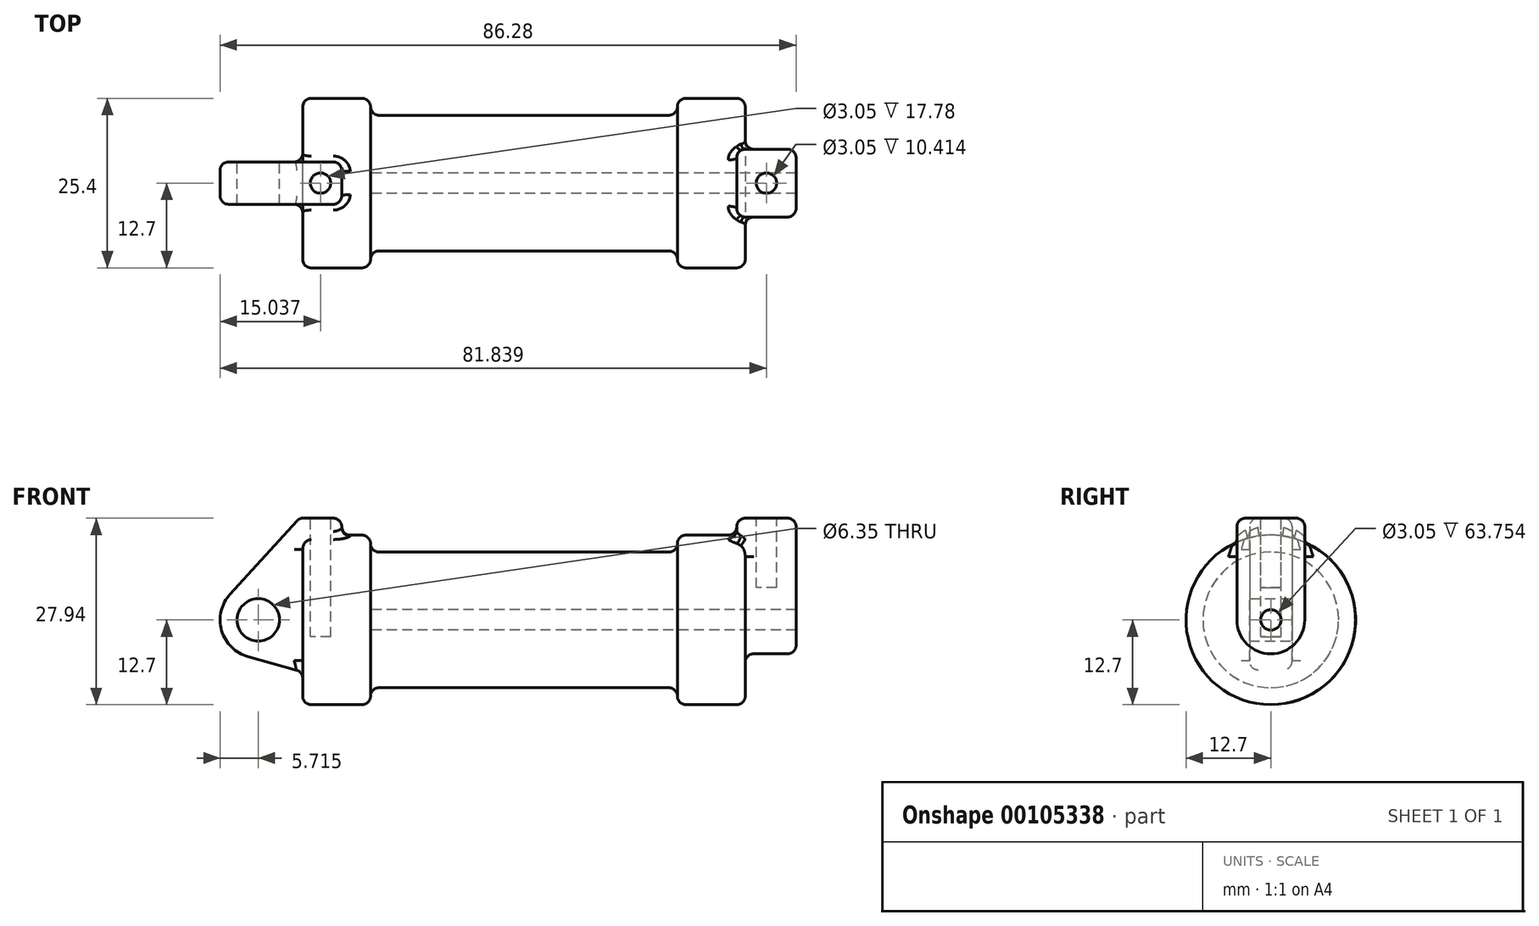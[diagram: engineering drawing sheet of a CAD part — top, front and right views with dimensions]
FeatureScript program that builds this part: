
annotation { "Feature Type Name" : "Feature", "Feature Type Description" : "" }
export const myFeature = defineFeature(function(context is Context, id is Id, definition is map)
    precondition{}
    {
        {
            var Q0;
            Q0=qCreatedBy(makeId("Front.planeOp"),FACE);
            var sketch = newSketch(context, id + "F0", { "sketchPlane" : qUnion([Q0])});
            skLineSegment(sketch, "E0", {"start": v(0, 0) * mm, "end": v(0, 12.7) * mm});
            skLineSegment(sketch, "E1", {"start": v(0, 12.7) * mm, "end": v(10.16, 12.7) * mm});
            skLineSegment(sketch, "E2", {"start": v(10.16, 12.7) * mm, "end": v(10.16, 10.16) * mm});
            skLineSegment(sketch, "E3", {"start": v(10.16, 10.16) * mm, "end": v(56.13, 10.16) * mm});
            skLineSegment(sketch, "E4", {"start": v(56.13, 10.16) * mm, "end": v(56.13, 12.7) * mm});
            skLineSegment(sketch, "E5", {"start": v(56.13, 12.7) * mm, "end": v(66.3, 12.7) * mm});
            skLineSegment(sketch, "E6", {"start": v(66.3, 12.7) * mm, "end": v(66.3, 0) * mm});
            skLineSegment(sketch, "E7", {"start": v(66.3, 0) * mm, "end": v(0, 0) * mm});
            skLineSegment(sketch, "E8", {"start": v(5.84, 15.24) * mm, "end": v(-0.5, 15.24) * mm});
            skLineSegment(sketch, "E9", {"start": v(-0.5, 15.24) * mm, "end": v(-10.88, 3.85) * mm});
            skLineSegment(sketch, "E10", {"start": v(0, 0) * mm, "end": v(-6.65, 0) * mm});
            skCircle(sketch, "E11", {"center": v(-6.65, 0) * mm, "radius": 5.72 * mm});
            skCircle(sketch, "E12", {"center": v(-6.65, 0) * mm, "radius": 3.18 * mm});
            skLineSegment(sketch, "E13", {"start": v(5.84, 15.24) * mm, "end": v(5.84, -9.4) * mm});
            skLineSegment(sketch, "E14", {"start": v(5.84, -9.4) * mm, "end": v(-8.18, -5.5) * mm});
            skSolve(sketch);
        }
        {
            var Q0;
            {var subQ0=sQuery(id+"F0.wireOp",EDGE,"E2");Q0=makeQuery(id+"F0.imprint","IMPRINT",FACE,{"disambiguationData":[TD([[makeQuery(id+"F0.imprint","IMPRINT",EDGE,{"derivedFrom":subQ0}),-1.0]])]});}
            var Q1;
            {var subQ0=sQuery(id+"F0.wireOp",EDGE,"E0");Q1=makeQuery(id+"F0.imprint","IMPRINT",FACE,{"disambiguationData":[TD([[makeQuery(id+"F0.imprint","IMPRINT",EDGE,{"derivedFrom":subQ0}),-1.0]])]});}
            var Q2;
            Q2=sQuery(id+"F0.wireOp",EDGE,"E7");
            revolve(context, id + "F1", {"entities" : qUnion([Q0, Q1]), "axis" : qUnion([Q2]), "revolveType" : RevolveType.FULL});
        }
        {
            var Q0;
            {var subQ3=sQuery(id+"F0.wireOp",EDGE,"E0");Q0=makeQuery(id+"F0.imprint","IMPRINT",FACE,{"disambiguationData":[TD([[makeQuery(id+"F0.imprint","IMPRINT",EDGE,{"derivedFrom":subQ3}),1.0]])]});}
            var Q1;
            {var subQ4=sQuery(id+"F0.wireOp",EDGE,"E12");Q1=makeQuery(id+"F0.imprint","IMPRINT",FACE,{"disambiguationData":[TD([[makeQuery(id+"F0.imprint","IMPRINT",EDGE,{"derivedFrom":subQ4}),-1.0]])]});}
            var Q2;
            {var subQ0=sQuery(id+"F0.wireOp",EDGE,"E14");Q2=makeQuery(id+"F0.imprint","IMPRINT",FACE,{"disambiguationData":[TD([[makeQuery(id+"F0.imprint","IMPRINT",EDGE,{"derivedFrom":subQ0}),-1.0]])]});}
            var Q3;
            {var subQ0=sQuery(id+"F0.wireOp",EDGE,"E0");Q3=makeQuery(id+"F0.imprint","IMPRINT",FACE,{"disambiguationData":[TD([[makeQuery(id+"F0.imprint","IMPRINT",EDGE,{"derivedFrom":subQ0}),-1.0]])]});}
            extrude(context, id + "F2", {"entities" : qUnion([Q0, Q1, Q2, Q3]), "operationType" : NewBodyOperationType.ADD, "endBound" : BoundingType.SYMMETRIC, "depth" : 6.35 * mm});
        }
        {
            var Q0;
            Q0=makeQuery(id+"F1.opRevolve","SWEPT_FACE",FACE,{"disambiguationData":[OSD([sQuery(id+"F0.wireOp",EDGE,"E6")])]});
            var sketch = newSketch(context, id + "F3", { "sketchPlane" : qUnion([Q0])});
            skCircle(sketch, "E15", {"center": v(0, 0) * mm, "radius": 1.52 * mm});
            skCircle(sketch, "E16", {"center": v(0, 0) * mm, "radius": 5.08 * mm});
            skLineSegment(sketch, "E17", {"start": v(5.08, 0) * mm, "end": v(5.08, 15.24) * mm});
            skLineSegment(sketch, "E18", {"start": v(-5.08, 0) * mm, "end": v(-5.08, 15.24) * mm});
            skLineSegment(sketch, "E19", {"start": v(-5.08, 15.24) * mm, "end": v(5.08, 15.24) * mm});
            skSolve(sketch);
        }
        {
            var Q0;
            {var subQ0=sQuery(id+"F3.wireOp",EDGE,"E19");Q0=makeQuery(id+"F3.imprint","IMPRINT",FACE,{"disambiguationData":[TD([[makeQuery(id+"F3.imprint","IMPRINT",EDGE,{"derivedFrom":subQ0}),-1.0]])]});}
            var Q1;
            {var subQ0=sQuery(id+"F3.wireOp",EDGE,"E17");var subQ1=sQuery(id+"F3.wireOp",EDGE,"E16");var subQ2=makeQuery(id+"F3.imprint","INTERSECT",VERTEX,{"derivedFrom":[subQ1,subQ0]});Q1=makeQuery(id+"F3.imprint","IMPRINT",FACE,{"disambiguationData":[TD([[makeQuery(id+"F3.imprint","IMPRINT",EDGE,{"disambiguationData":[TD([[subQ2,-1.0]])],"derivedFrom":subQ1}),-1.0]])]});}
            var Q2;
            Q2=makeQuery(id+"F3.imprint","IMPRINT",FACE,{"disambiguationData":[TD([[makeQuery(id+"F3.imprint","IMPRINT",EDGE,{"derivedFrom":sQuery(id+"F3.wireOp",EDGE,"E15")}),-1.0]])]});
            extrude(context, id + "F4", {"entities" : qUnion([Q0, Q1, Q2]), "depth" : 7.62 * mm, "hasSecondDirection" : true, "secondDirectionOppositeDirection" : true, "secondDirectionDepth" : 1.27 * mm});
        }
        {
            var Q0;
            Q0=makeQuery(id+"F4.opExtrude","SWEPT_BODY",BODY,{"disambiguationData":[OSD([sQuery(id+"F3.wireOp",EDGE,"E15"),sQuery(id+"F3.wireOp",EDGE,"E16"),sQuery(id+"F3.wireOp",EDGE,"E17"),sQuery(id+"F3.wireOp",EDGE,"E18"),sQuery(id+"F3.wireOp",EDGE,"E19")])]});
            var Q1;
            Q1=makeQuery(id+"F1.opRevolve","SWEPT_BODY",BODY,{"disambiguationData":[OSD([sQuery(id+"F0.wireOp",EDGE,"E0"),sQuery(id+"F0.wireOp",EDGE,"E1"),sQuery(id+"F0.wireOp",EDGE,"E2"),sQuery(id+"F0.wireOp",EDGE,"E3"),sQuery(id+"F0.wireOp",EDGE,"E4"),sQuery(id+"F0.wireOp",EDGE,"E5"),sQuery(id+"F0.wireOp",EDGE,"E6"),sQuery(id+"F0.wireOp",EDGE,"E7")])]});
            booleanBodies(context, id + "F5", {"operationType" : BooleanOperationType.UNION, "tools" : qUnion([Q0, Q1])});
        }
        {
            var Q0;
            Q0=makeQuery(id+"F3.imprint","IMPRINT",FACE,{"disambiguationData":[TD([[makeQuery(id+"F3.imprint","IMPRINT",EDGE,{"derivedFrom":sQuery(id+"F3.wireOp",EDGE,"E15")}),1.0]])]});
            var Q1;
            Q1=makeQuery(id+"F1.opRevolve","SWEPT_FACE",FACE,{"disambiguationData":[OSD([sQuery(id+"F0.wireOp",EDGE,"E2")])]});
            extrude(context, id + "F6", {"entities" : qUnion([Q0]), "operationType" : NewBodyOperationType.REMOVE, "endBound" : BoundingType.UP_TO_SURFACE, "oppositeDirection" : true, "endBoundEntityFace" : qUnion([Q1]), "depth" : 25.4 * mm});
        }
        {
            var Q0;
            Q0=makeQuery(id+"F4.opExtrude","SWEPT_FACE",FACE,{"disambiguationData":[OSD([sQuery(id+"F3.wireOp",EDGE,"E19")])]});
            var sketch = newSketch(context, id + "F7", { "sketchPlane" : qUnion([Q0])});
            skLineSegment(sketch, "E20", {"start": v(65.02, 0) * mm, "end": v(73.91, 0) * mm, "construction": true});
            skLineSegment(sketch, "E21", {"start": v(69.47, 5.08) * mm, "end": v(69.47, -5.08) * mm, "construction": true});
            skCircle(sketch, "E22", {"center": v(69.47, 0) * mm, "radius": 1.52 * mm});
            skLineSegment(sketch, "E23.0.0", {"start": v(5.84, 3.18) * mm, "end": v(-0.5, 3.18) * mm});
            skLineSegment(sketch, "E23.0.1", {"start": v(-0.5, 3.17) * mm, "end": v(-0.5, -3.18) * mm});
            skLineSegment(sketch, "E23.0.2", {"start": v(-0.5, -3.18) * mm, "end": v(5.84, -3.18) * mm});
            skLineSegment(sketch, "E23.0.3", {"start": v(5.84, -3.18) * mm, "end": v(5.84, 3.17) * mm});
            skLineSegment(sketch, "E24", {"start": v(-0.5, 0) * mm, "end": v(5.84, 0) * mm, "construction": true});
            skLineSegment(sketch, "E25", {"start": v(2.67, 3.18) * mm, "end": v(2.67, -3.18) * mm, "construction": true});
            skCircle(sketch, "E26", {"center": v(2.67, 0) * mm, "radius": 1.52 * mm});
            skSolve(sketch);
        }
        {
            var Q0;
            Q0=makeQuery(id+"F7.imprint","IMPRINT",FACE,{"disambiguationData":[TD([[makeQuery(id+"F7.imprint","IMPRINT",EDGE,{"derivedFrom":sQuery(id+"F7.wireOp",EDGE,"E26")}),1.0]])]});
            var Q1;
            Q1=sQuery(id+"F7.wireOp",EDGE,"E26");
            extrude(context, id + "F8", {"entities" : qUnion([Q0]), "operationType" : NewBodyOperationType.REMOVE, "surfaceEntities" : qUnion([Q1]), "oppositeDirection" : true, "depth" : 17.78 * mm});
        }
        {
            var Q0;
            Q0=makeQuery(id+"F7.imprint","IMPRINT",FACE,{"disambiguationData":[TD([[makeQuery(id+"F7.imprint","IMPRINT",EDGE,{"derivedFrom":sQuery(id+"F7.wireOp",EDGE,"E22")}),1.0]])]});
            var Q1;
            Q1=sQuery(id+"F7.wireOp",EDGE,"E22");
            extrude(context, id + "F9", {"entities" : qUnion([Q0]), "operationType" : NewBodyOperationType.REMOVE, "surfaceEntities" : qUnion([Q1]), "oppositeDirection" : true, "depth" : 10.4 * mm});
        }
        {
            var Q0;
            Q0=makeQuery(id+"F1.opRevolve","SWEPT_EDGE",EDGE,{"disambiguationData":[OSD([sQuery(id+"F0.wireOp",EDGE,"E2"),sQuery(id+"F0.wireOp",EDGE,"E3")])]});
            var Q1;
            Q1=makeQuery(id+"F1.opRevolve","SWEPT_EDGE",EDGE,{"disambiguationData":[OSD([sQuery(id+"F0.wireOp",EDGE,"E3"),sQuery(id+"F0.wireOp",EDGE,"E4")])]});
            var Q2;
            Q2=makeQuery(id+"F1.opRevolve","SWEPT_EDGE",EDGE,{"disambiguationData":[OSD([sQuery(id+"F0.wireOp",EDGE,"E5"),sQuery(id+"F0.wireOp",EDGE,"E6")])]});
            var Q3;
            Q3=makeQuery(id+"F1.opRevolve","SWEPT_EDGE",EDGE,{"disambiguationData":[OSD([sQuery(id+"F0.wireOp",EDGE,"E0"),sQuery(id+"F0.wireOp",EDGE,"E1")])]});
            var Q4;
            Q4=makeQuery(id+"F1.opRevolve","SWEPT_EDGE",EDGE,{"disambiguationData":[OSD([sQuery(id+"F0.wireOp",EDGE,"E1"),sQuery(id+"F0.wireOp",EDGE,"E2")])]});
            var Q5;
            Q5=makeQuery(id+"F1.opRevolve","SWEPT_EDGE",EDGE,{"disambiguationData":[OSD([sQuery(id+"F0.wireOp",EDGE,"E4"),sQuery(id+"F0.wireOp",EDGE,"E5")])]});
            fillet(context, id + "F10", {"entities" : qUnion([Q0, Q1, Q2, Q3, Q4, Q5]), "radius" : 1.27 * mm, "tangentPropagation" : true, "allowEdgeOverflow" : false});
        }
        {
            var Q0;
            Q0=makeQuery(id+"F2.opExtrude","CAP_EDGE",EDGE,{"disambiguationData":[OSD([sQuery(id+"F0.wireOp",EDGE,"E9")])],"isStart":false});
            var Q1;
            Q1=makeQuery(id+"F2.opExtrude","SWEPT_EDGE",EDGE,{"disambiguationData":[OSD([sQuery(id+"F0.wireOp",EDGE,"E8"),sQuery(id+"F0.wireOp",EDGE,"E9")])]});
            var Q2;
            Q2=makeQuery(id+"F2.opExtrude","CAP_EDGE",EDGE,{"disambiguationData":[OSD([sQuery(id+"F0.wireOp",EDGE,"E8")])],"isStart":true});
            var Q3;
            Q3=makeQuery(id+"F2.opExtrude","SWEPT_EDGE",EDGE,{"disambiguationData":[OSD([sQuery(id+"F0.wireOp",EDGE,"E8"),sQuery(id+"F0.wireOp",EDGE,"E13")])]});
            var Q4;
            Q4=makeQuery(id+"F2.opExtrude","CAP_EDGE",EDGE,{"disambiguationData":[OSD([sQuery(id+"F0.wireOp",EDGE,"E8")])],"isStart":false});
            var Q5;
            Q5=makeQuery(id+"F2.opExtrude","CAP_EDGE",EDGE,{"disambiguationData":[OSD([sQuery(id+"F0.wireOp",EDGE,"E9")])],"isStart":true});
            var Q6;
            Q6=makeQuery(id+"F2.opExtrude","CAP_EDGE",EDGE,{"disambiguationData":[OSD([sQuery(id+"F0.wireOp",EDGE,"E11")])],"isStart":false});
            var Q7;
            Q7=makeQuery(id+"F2.opExtrude","CAP_EDGE",EDGE,{"disambiguationData":[OSD([sQuery(id+"F0.wireOp",EDGE,"E14")])],"isStart":false});
            var Q8;
            Q8=makeQuery(id+"F2.opExtrude","CAP_EDGE",EDGE,{"disambiguationData":[OSD([sQuery(id+"F0.wireOp",EDGE,"E11")])],"isStart":true});
            var Q9;
            Q9=makeQuery(id+"F2.opExtrude","CAP_EDGE",EDGE,{"disambiguationData":[OSD([sQuery(id+"F0.wireOp",EDGE,"E14")])],"isStart":true});
            var Q10;
            Q10=makeQuery(id+"F10.opFillet","BLEND_EDGE",EDGE,{"blendedFrom":[makeQuery(id+"F1.opRevolve","SWEPT_EDGE",EDGE,{"disambiguationData":[OSD([sQuery(id+"F0.wireOp",EDGE,"E0"),sQuery(id+"F0.wireOp",EDGE,"E1")])]}),makeQuery(id+"F2.opExtrude","CAP_FACE",FACE,{"disambiguationData":[OSD([sQuery(id+"F0.wireOp",EDGE,"E8"),sQuery(id+"F0.wireOp",EDGE,"E9"),sQuery(id+"F0.wireOp",EDGE,"E11"),sQuery(id+"F0.wireOp",EDGE,"E12"),sQuery(id+"F0.wireOp",EDGE,"E13"),sQuery(id+"F0.wireOp",EDGE,"E14")])],"isStart":false})],"blendedInto":[makeQuery(id+"F2.opExtrude","CAP_FACE",FACE,{"disambiguationData":[OSD([sQuery(id+"F0.wireOp",EDGE,"E8"),sQuery(id+"F0.wireOp",EDGE,"E9"),sQuery(id+"F0.wireOp",EDGE,"E11"),sQuery(id+"F0.wireOp",EDGE,"E12"),sQuery(id+"F0.wireOp",EDGE,"E13"),sQuery(id+"F0.wireOp",EDGE,"E14")])],"isStart":false})]});
            var Q11;
            Q11=makeQuery(id+"F2.boolean.opBoolean","INTERSECT",EDGE,{"derivedFrom":[makeQuery(id+"F1.opRevolve","SWEPT_FACE",FACE,{"disambiguationData":[OSD([sQuery(id+"F0.wireOp",EDGE,"E1")])]}),makeQuery(id+"F2.opExtrude","SWEPT_FACE",FACE,{"disambiguationData":[OSD([sQuery(id+"F0.wireOp",EDGE,"E13")])]})]});
            var Q12;
            Q12=makeQuery(id+"F2.boolean.opBoolean","INTERSECT",EDGE,{"derivedFrom":[makeQuery(id+"F1.opRevolve","SWEPT_FACE",FACE,{"disambiguationData":[OSD([sQuery(id+"F0.wireOp",EDGE,"E1")])]}),makeQuery(id+"F2.opExtrude","CAP_FACE",FACE,{"disambiguationData":[OSD([sQuery(id+"F0.wireOp",EDGE,"E8"),sQuery(id+"F0.wireOp",EDGE,"E9"),sQuery(id+"F0.wireOp",EDGE,"E11"),sQuery(id+"F0.wireOp",EDGE,"E12"),sQuery(id+"F0.wireOp",EDGE,"E13"),sQuery(id+"F0.wireOp",EDGE,"E14")])],"isStart":false})]});
            var Q13;
            Q13=makeQuery(id+"F2.boolean.opBoolean","INTERSECT",EDGE,{"derivedFrom":[makeQuery(id+"F1.opRevolve","SWEPT_FACE",FACE,{"disambiguationData":[OSD([sQuery(id+"F0.wireOp",EDGE,"E0")])]}),makeQuery(id+"F2.opExtrude","CAP_FACE",FACE,{"disambiguationData":[OSD([sQuery(id+"F0.wireOp",EDGE,"E8"),sQuery(id+"F0.wireOp",EDGE,"E9"),sQuery(id+"F0.wireOp",EDGE,"E11"),sQuery(id+"F0.wireOp",EDGE,"E12"),sQuery(id+"F0.wireOp",EDGE,"E13"),sQuery(id+"F0.wireOp",EDGE,"E14")])],"isStart":false})]});
            var Q14;
            Q14=makeQuery(id+"F2.boolean.opBoolean","INTERSECT",EDGE,{"derivedFrom":[makeQuery(id+"F1.opRevolve","SWEPT_FACE",FACE,{"disambiguationData":[OSD([sQuery(id+"F0.wireOp",EDGE,"E1")])]}),makeQuery(id+"F2.opExtrude","CAP_FACE",FACE,{"disambiguationData":[OSD([sQuery(id+"F0.wireOp",EDGE,"E8"),sQuery(id+"F0.wireOp",EDGE,"E9"),sQuery(id+"F0.wireOp",EDGE,"E11"),sQuery(id+"F0.wireOp",EDGE,"E12"),sQuery(id+"F0.wireOp",EDGE,"E13"),sQuery(id+"F0.wireOp",EDGE,"E14")])],"isStart":true})]});
            var Q15;
            Q15=makeQuery(id+"F10.opFillet","BLEND_EDGE",EDGE,{"blendedFrom":[makeQuery(id+"F1.opRevolve","SWEPT_EDGE",EDGE,{"disambiguationData":[OSD([sQuery(id+"F0.wireOp",EDGE,"E0"),sQuery(id+"F0.wireOp",EDGE,"E1")])]}),makeQuery(id+"F2.opExtrude","CAP_FACE",FACE,{"disambiguationData":[OSD([sQuery(id+"F0.wireOp",EDGE,"E8"),sQuery(id+"F0.wireOp",EDGE,"E9"),sQuery(id+"F0.wireOp",EDGE,"E11"),sQuery(id+"F0.wireOp",EDGE,"E12"),sQuery(id+"F0.wireOp",EDGE,"E13"),sQuery(id+"F0.wireOp",EDGE,"E14")])],"isStart":true})],"blendedInto":[makeQuery(id+"F2.opExtrude","CAP_FACE",FACE,{"disambiguationData":[OSD([sQuery(id+"F0.wireOp",EDGE,"E8"),sQuery(id+"F0.wireOp",EDGE,"E9"),sQuery(id+"F0.wireOp",EDGE,"E11"),sQuery(id+"F0.wireOp",EDGE,"E12"),sQuery(id+"F0.wireOp",EDGE,"E13"),sQuery(id+"F0.wireOp",EDGE,"E14")])],"isStart":true})]});
            var Q16;
            Q16=makeQuery(id+"F2.boolean.opBoolean","INTERSECT",EDGE,{"derivedFrom":[makeQuery(id+"F1.opRevolve","SWEPT_FACE",FACE,{"disambiguationData":[OSD([sQuery(id+"F0.wireOp",EDGE,"E0")])]}),makeQuery(id+"F2.opExtrude","CAP_FACE",FACE,{"disambiguationData":[OSD([sQuery(id+"F0.wireOp",EDGE,"E8"),sQuery(id+"F0.wireOp",EDGE,"E9"),sQuery(id+"F0.wireOp",EDGE,"E11"),sQuery(id+"F0.wireOp",EDGE,"E12"),sQuery(id+"F0.wireOp",EDGE,"E13"),sQuery(id+"F0.wireOp",EDGE,"E14")])],"isStart":true})]});
            var Q17;
            Q17=makeQuery(id+"F2.opExtrude","CAP_EDGE",EDGE,{"disambiguationData":[OSD([sQuery(id+"F0.wireOp",EDGE,"E13")])],"isStart":false});
            var Q18;
            Q18=makeQuery(id+"F2.opExtrude","CAP_EDGE",EDGE,{"disambiguationData":[OSD([sQuery(id+"F0.wireOp",EDGE,"E13")])],"isStart":true});
            var Q19;
            Q19=makeQuery(id+"F2.boolean.opBoolean","INTERSECT",EDGE,{"derivedFrom":[makeQuery(id+"F1.opRevolve","SWEPT_FACE",FACE,{"disambiguationData":[OSD([sQuery(id+"F0.wireOp",EDGE,"E0")])]}),makeQuery(id+"F2.opExtrude","SWEPT_FACE",FACE,{"disambiguationData":[OSD([sQuery(id+"F0.wireOp",EDGE,"E14")])]})]});
            var Q20;
            Q20=makeQuery(id+"F2.opExtrude","SWEPT_EDGE",EDGE,{"disambiguationData":[OSD([sQuery(id+"F0.wireOp",EDGE,"E9"),sQuery(id+"F0.wireOp",EDGE,"E11")])]});
            var Q21;
            Q21=makeQuery(id+"F2.opExtrude","SWEPT_EDGE",EDGE,{"disambiguationData":[OSD([sQuery(id+"F0.wireOp",EDGE,"E11"),sQuery(id+"F0.wireOp",EDGE,"E14")])]});
            fillet(context, id + "F11", {"entities" : qUnion([Q0, Q1, Q2, Q3, Q4, Q5, Q6, Q7, Q8, Q9, Q10, Q11, Q12, Q13, Q14, Q15, Q16, Q17, Q18, Q19, Q20, Q21]), "radius" : 1.27 * mm, "tangentPropagation" : true, "allowEdgeOverflow" : false});
        }
        {
            var Q0;
            Q0=makeQuery(id+"F4.opExtrude","SWEPT_EDGE",EDGE,{"disambiguationData":[OSD([sQuery(id+"F3.wireOp",EDGE,"E18"),sQuery(id+"F3.wireOp",EDGE,"E19")])]});
            var Q1;
            Q1=makeQuery(id+"F4.opExtrude","CAP_EDGE",EDGE,{"disambiguationData":[OSD([sQuery(id+"F3.wireOp",EDGE,"E19")])],"isStart":false});
            var Q2;
            Q2=makeQuery(id+"F4.opExtrude","SWEPT_EDGE",EDGE,{"disambiguationData":[OSD([sQuery(id+"F3.wireOp",EDGE,"E17"),sQuery(id+"F3.wireOp",EDGE,"E19")])]});
            var Q3;
            Q3=makeQuery(id+"F4.opExtrude","CAP_EDGE",EDGE,{"disambiguationData":[OSD([sQuery(id+"F3.wireOp",EDGE,"E19")])],"isStart":true});
            var Q4;
            Q4=makeQuery(id+"F4.opExtrude","CAP_EDGE",EDGE,{"disambiguationData":[OSD([sQuery(id+"F3.wireOp",EDGE,"E18")])],"isStart":false});
            var Q5;
            Q5=makeQuery(id+"F4.opExtrude","CAP_EDGE",EDGE,{"disambiguationData":[OSD([sQuery(id+"F3.wireOp",EDGE,"E17")])],"isStart":false});
            var Q6;
            Q6=makeQuery(id+"F5.opBoolean","INTERSECT",EDGE,{"derivedFrom":[makeQuery(id+"F1.opRevolve","SWEPT_FACE",FACE,{"disambiguationData":[OSD([sQuery(id+"F0.wireOp",EDGE,"E6")])]}),makeQuery(id+"F4.opExtrude","SWEPT_FACE",FACE,{"disambiguationData":[OSD([sQuery(id+"F3.wireOp",EDGE,"E16")])]})]});
            var Q7;
            Q7=makeQuery(id+"F4.opExtrude","CAP_EDGE",EDGE,{"disambiguationData":[OSD([sQuery(id+"F3.wireOp",EDGE,"E16")])],"isStart":false});
            var Q8;
            Q8=makeQuery(id+"F5.opBoolean","INTERSECT",EDGE,{"derivedFrom":[makeQuery(id+"F1.opRevolve","SWEPT_FACE",FACE,{"disambiguationData":[OSD([sQuery(id+"F0.wireOp",EDGE,"E6")])]}),makeQuery(id+"F4.opExtrude","SWEPT_FACE",FACE,{"disambiguationData":[OSD([sQuery(id+"F3.wireOp",EDGE,"E17")])]})]});
            var Q9;
            Q9=makeQuery(id+"F5.opBoolean","INTERSECT",EDGE,{"derivedFrom":[makeQuery(id+"F1.opRevolve","SWEPT_FACE",FACE,{"disambiguationData":[OSD([sQuery(id+"F0.wireOp",EDGE,"E6")])]}),makeQuery(id+"F4.opExtrude","SWEPT_FACE",FACE,{"disambiguationData":[OSD([sQuery(id+"F3.wireOp",EDGE,"E18")])]})]});
            var Q10;
            Q10=makeQuery(id+"F5.opBoolean","INTERSECT",EDGE,{"derivedFrom":[makeQuery(id+"F1.opRevolve","SWEPT_FACE",FACE,{"disambiguationData":[OSD([sQuery(id+"F0.wireOp",EDGE,"E5")])]}),makeQuery(id+"F4.opExtrude","CAP_FACE",FACE,{"disambiguationData":[OSD([sQuery(id+"F3.wireOp",EDGE,"E15"),sQuery(id+"F3.wireOp",EDGE,"E16"),sQuery(id+"F3.wireOp",EDGE,"E17"),sQuery(id+"F3.wireOp",EDGE,"E18"),sQuery(id+"F3.wireOp",EDGE,"E19")])],"isStart":true})]});
            var Q11;
            Q11=makeQuery(id+"F10.opFillet","BLEND_EDGE",EDGE,{"blendedFrom":[makeQuery(id+"F1.opRevolve","SWEPT_EDGE",EDGE,{"disambiguationData":[OSD([sQuery(id+"F0.wireOp",EDGE,"E5"),sQuery(id+"F0.wireOp",EDGE,"E6")])]}),makeQuery(id+"F4.opExtrude","SWEPT_FACE",FACE,{"disambiguationData":[OSD([sQuery(id+"F3.wireOp",EDGE,"E18")])]})],"blendedInto":[makeQuery(id+"F4.opExtrude","SWEPT_FACE",FACE,{"disambiguationData":[OSD([sQuery(id+"F3.wireOp",EDGE,"E18")])]})]});
            var Q12;
            Q12=makeQuery(id+"F4.opExtrude","SWEPT_EDGE",EDGE,{"disambiguationData":[OSD([sQuery(id+"F3.wireOp",EDGE,"E16"),sQuery(id+"F3.wireOp",EDGE,"E18")])]});
            var Q13;
            Q13=makeQuery(id+"F10.opFillet","BLEND_EDGE",EDGE,{"blendedFrom":[makeQuery(id+"F1.opRevolve","SWEPT_EDGE",EDGE,{"disambiguationData":[OSD([sQuery(id+"F0.wireOp",EDGE,"E5"),sQuery(id+"F0.wireOp",EDGE,"E6")])]}),makeQuery(id+"F4.opExtrude","SWEPT_FACE",FACE,{"disambiguationData":[OSD([sQuery(id+"F3.wireOp",EDGE,"E17")])]})],"blendedInto":[makeQuery(id+"F4.opExtrude","SWEPT_FACE",FACE,{"disambiguationData":[OSD([sQuery(id+"F3.wireOp",EDGE,"E17")])]})]});
            var Q14;
            Q14=makeQuery(id+"F4.opExtrude","CAP_EDGE",EDGE,{"disambiguationData":[OSD([sQuery(id+"F3.wireOp",EDGE,"E17")])],"isStart":true});
            var Q15;
            Q15=makeQuery(id+"F4.opExtrude","CAP_EDGE",EDGE,{"disambiguationData":[OSD([sQuery(id+"F3.wireOp",EDGE,"E18")])],"isStart":true});
            fillet(context, id + "F12", {"entities" : qUnion([Q0, Q1, Q2, Q3, Q4, Q5, Q6, Q7, Q8, Q9, Q10, Q11, Q12, Q13, Q14, Q15]), "radius" : 1.27 * mm, "tangentPropagation" : true, "allowEdgeOverflow" : false});
        }
    });
